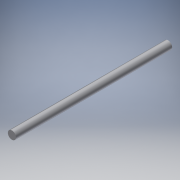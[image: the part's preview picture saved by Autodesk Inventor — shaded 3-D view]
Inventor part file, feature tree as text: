
AUTODESK INVENTOR PART (.ipt)
format: ipt  version: 2017.1 (Build 211199000, 199)  size: 99,328 bytes
history: native  units: in
note: dims shown in document units (in); Inventor stores cm internally (conversion verified against a paired STEP export)
features: extrude x1, sketch x1
ambient origin geometry x8: Origin, YZ Plane, XZ Plane, XY Plane, X Axis, Y Axis, Z Axis, Center Point
bodies: Solid1 (feature_tree)
feature tree (2):
  extrude  "Extrusion1"  Depth=12.0in TaperAngle=0.0deg
  sketch  "Sketch1"  dims[d0=0.625in d1=12.0in d2=0.0in]
